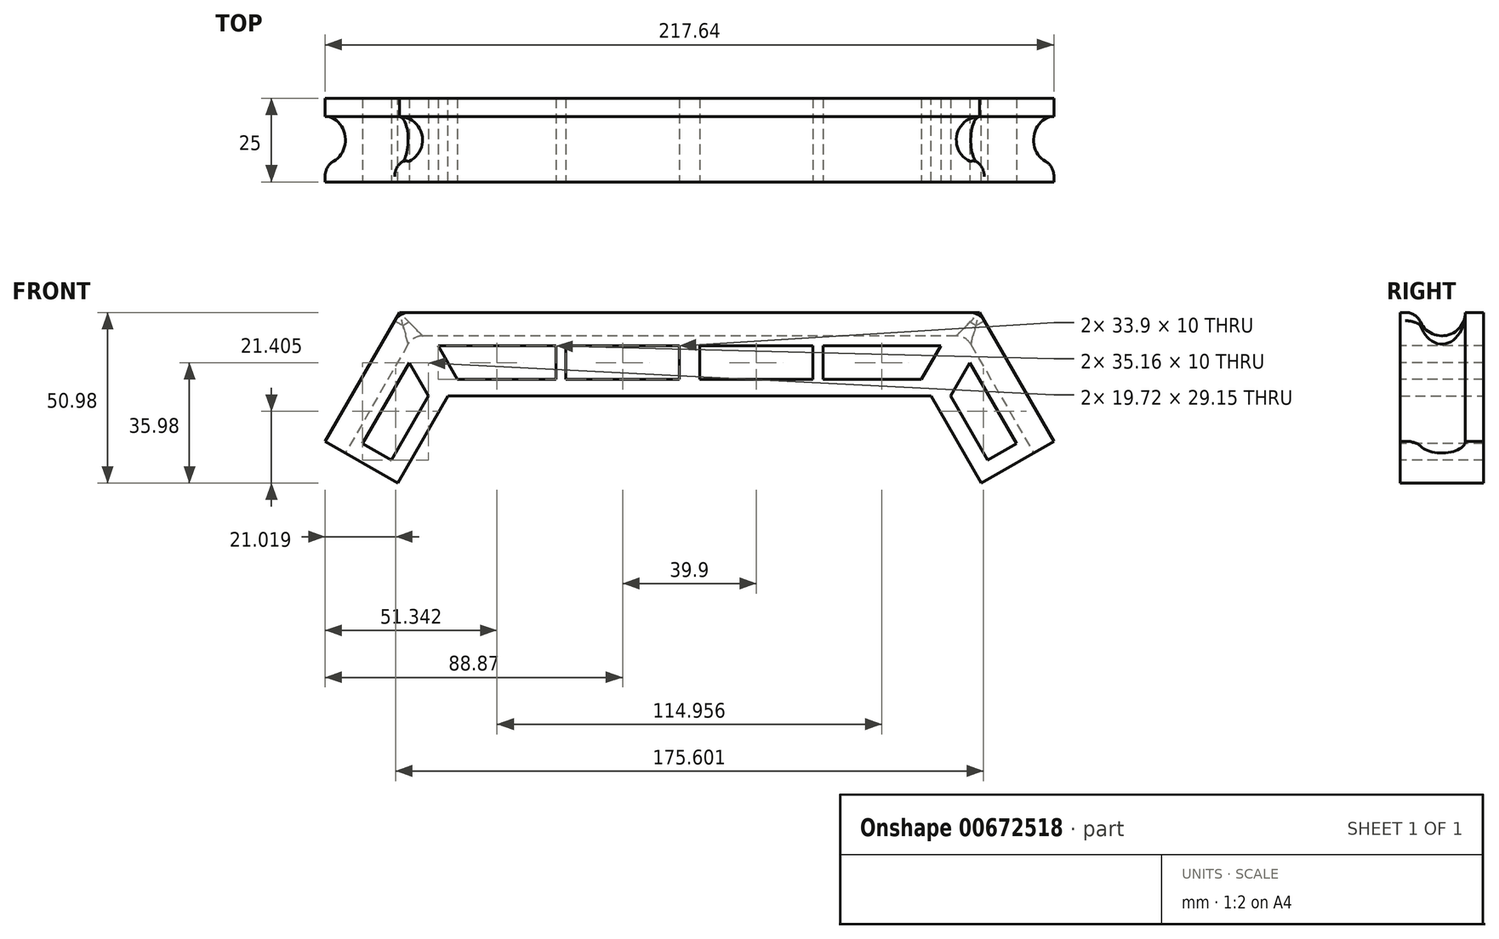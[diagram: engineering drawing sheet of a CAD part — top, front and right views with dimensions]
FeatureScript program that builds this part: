
annotation { "Feature Type Name" : "Feature", "Feature Type Description" : "" }
export const myFeature = defineFeature(function(context is Context, id is Id, definition is map)
    precondition{}
    {
        {
            var Q0;
            Q0=qCreatedBy(makeId("Front.planeOp"),FACE);
            var sketch = newSketch(context, id + "F0", { "sketchPlane" : qUnion([Q0])});
            skCircle(sketch, "E0.cCircle", {"center": v(0, 0) * mm, "radius": 150 * mm, "construction": true});
            skLineSegment(sketch, "E0.0", {"start": v(-86.6, 150) * mm, "end": v(86.6, 150) * mm});
            skLineSegment(sketch, "E0.1", {"start": v(86.6, 150) * mm, "end": v(173.2, 0) * mm});
            skLineSegment(sketch, "E0.2", {"start": v(173.2, 0) * mm, "end": v(86.6, -150) * mm});
            skLineSegment(sketch, "E0.3", {"start": v(86.6, -150) * mm, "end": v(-86.6, -150) * mm});
            skLineSegment(sketch, "E0.4", {"start": v(-86.6, -150) * mm, "end": v(-173.2, 0) * mm});
            skLineSegment(sketch, "E0.5", {"start": v(-173.2, 0) * mm, "end": v(-86.6, 150) * mm});
            skPoint(sketch, "E0.0.midPoint", {"position": v(0, 150) * mm});
            skLineSegment(sketch, "E1.0", {"start": v(72.17, 125) * mm, "end": v(151.55, -12.5) * mm});
            skLineSegment(sketch, "E1.1", {"start": v(-72.17, 125) * mm, "end": v(72.17, 125) * mm});
            skLineSegment(sketch, "E1.2", {"start": v(-151.55, -12.5) * mm, "end": v(-72.17, 125) * mm});
            skLineSegment(sketch, "E2", {"start": v(-87.17, 99.02) * mm, "end": v(-117.44, 116.5) * mm});
            skLineSegment(sketch, "E3", {"start": v(0, 150) * mm, "end": v(0, 125) * mm});
            skSolve(sketch);
        }
        {
            var Q0;
            {var subQ5=sQuery(id+"F0.wireOp",EDGE,"E3");Q0=makeQuery(id+"F0.imprint","IMPRINT",FACE,{"disambiguationData":[TD([[makeQuery(id+"F0.imprint","IMPRINT",EDGE,{"derivedFrom":subQ5}),-1.0]])]});}
            extrude(context, id + "F1", {"entities" : qUnion([Q0]), "depth" : 25 * mm, "offsetDistance" : 25 * mm});
        }
        {
            var Q0;
            Q0=makeQuery(id+"F1.opExtrude","SWEPT_FACE",FACE,{"disambiguationData":[OSD([sQuery(id+"F0.wireOp",EDGE,"E3")])]});
            var sketch = newSketch(context, id + "F2", { "sketchPlane" : qUnion([Q0])});
            skCircle(sketch, "E4", {"center": v(-12.5, 150) * mm, "radius": 7 * mm});
            skPoint(sketch, "E4.centerSnap0", {"position": v(-12.5, 150) * mm});
            skSolve(sketch);
        }
        {
            var Q0;
            {var subQ0=sQuery(id+"F2.wireOp",EDGE,"E4");var subQ1=makeQuery(id+"F1.opExtrude","SWEPT_EDGE",EDGE,{"disambiguationData":[OSD([sQuery(id+"F0.wireOp",EDGE,"E0.0"),sQuery(id+"F0.wireOp",EDGE,"E3")])]});var subQ2=makeQuery(id+"F2.imprint","INTERSECT",VERTEX,{"disambiguationData":[OD(0.0)],"derivedFrom":[subQ1,subQ0]});Q0=makeQuery(id+"F2.imprint","IMPRINT",FACE,{"disambiguationData":[TD([[makeQuery(id+"F2.imprint","IMPRINT",EDGE,{"disambiguationData":[TD([[subQ2,1.0]])],"derivedFrom":subQ0}),1.0]])]});}
            var Q1;
            Q1=makeQuery(id+"F1.opExtrude","CAP_EDGE",EDGE,{"disambiguationData":[OSD([sQuery(id+"F0.wireOp",EDGE,"E0.0")])],"isStart":false});
            var Q2;
            Q2=makeQuery(id+"F1.opExtrude","CAP_EDGE",EDGE,{"disambiguationData":[OSD([sQuery(id+"F0.wireOp",EDGE,"E0.5")])],"isStart":false});
            sweep(context, id + "F3", {"operationType" : NewBodyOperationType.REMOVE, "profiles" : qUnion([Q0]), "path" : qUnion([Q1, Q2])});
        }
        {
            var Q0;
            {var subQ0=makeQuery(id+"F1.opExtrude","CAP_FACE",FACE,{"disambiguationData":[OSD([sQuery(id+"F0.wireOp",EDGE,"E0.0"),sQuery(id+"F0.wireOp",EDGE,"E0.5"),sQuery(id+"F0.wireOp",EDGE,"E1.1"),sQuery(id+"F0.wireOp",EDGE,"E1.2"),sQuery(id+"F0.wireOp",EDGE,"E2"),sQuery(id+"F0.wireOp",EDGE,"E3")])],"isStart":false});Q0=makeQuery(id+"F6.boolean.opBoolean","MERGE",FACE,{"derivedFrom":[subQ0,makeQuery(id+"F6.opPattern","COPY",FACE,{"derivedFrom":subQ0,"instanceName":"1"})]});}
            var sketch = newSketch(context, id + "F4", { "sketchPlane" : qUnion([Q0])});
            skLineSegment(sketch, "E5", {"start": v(-86.6, 150) * mm, "end": v(-72.17, 125) * mm});
            skLineSegment(sketch, "E6.0", {"start": v(-82.27, 152.5) * mm, "end": v(-67.84, 127.5) * mm});
            skLineSegment(sketch, "E7.0", {"start": v(-70.4, 130) * mm, "end": v(70.4, 130) * mm});
            skLineSegment(sketch, "E8.0", {"start": v(-84.88, 140) * mm, "end": v(84.88, 140) * mm});
            skLineSegment(sketch, "E9", {"start": v(0, 140) * mm, "end": v(0, 130) * mm});
            skLineSegment(sketch, "E10", {"start": v(0, 130) * mm, "end": v(-3, 130) * mm});
            skLineSegment(sketch, "E11", {"start": v(-3, 130) * mm, "end": v(-3, 140) * mm});
            skLineSegment(sketch, "E12", {"start": v(-3, 140) * mm, "end": v(0, 140) * mm});
            skLineSegment(sketch, "E13", {"start": v(-36.9, 140) * mm, "end": v(-36.9, 130) * mm});
            skLineSegment(sketch, "E14", {"start": v(-36.9, 130) * mm, "end": v(-39.9, 130) * mm});
            skLineSegment(sketch, "E15", {"start": v(-39.9, 130) * mm, "end": v(-39.9, 140) * mm});
            skLineSegment(sketch, "E16", {"start": v(-39.9, 140) * mm, "end": v(-36.9, 140) * mm});
            skLineSegment(sketch, "E17.0", {"start": v(-84.67, 103.35) * mm, "end": v(-114.94, 120.82) * mm});
            skLineSegment(sketch, "E18.0", {"start": v(-155.88, -10) * mm, "end": v(-75.06, 130) * mm});
            skLineSegment(sketch, "E19", {"start": v(-75.06, 130) * mm, "end": v(-70.4, 130) * mm});
            skLineSegment(sketch, "E20", {"start": v(-80.83, 140) * mm, "end": v(-97.66, 110.85) * mm});
            skLineSegment(sketch, "E21.0", {"start": v(-90.93, 147.5) * mm, "end": v(-76.5, 122.5) * mm});
            skSolve(sketch);
        }
        {
            var Q0;
            {var subQ0=sQuery(id+"F4.wireOp",EDGE,"E20");var subQ1=sQuery(id+"F4.wireOp",EDGE,"E17.0");var subQ2=makeQuery(id+"F4.imprint","INTERSECT",VERTEX,{"derivedFrom":[subQ1,subQ0]});Q0=makeQuery(id+"F4.imprint","IMPRINT",FACE,{"disambiguationData":[TD([[makeQuery(id+"F4.imprint","IMPRINT",EDGE,{"disambiguationData":[TD([[subQ2,1.0]])],"derivedFrom":subQ1}),-1.0]])]});}
            var Q1;
            {var subQ5=sQuery(id+"F4.wireOp",EDGE,"E15");Q1=makeQuery(id+"F4.imprint","IMPRINT",FACE,{"disambiguationData":[TD([[makeQuery(id+"F4.imprint","IMPRINT",EDGE,{"derivedFrom":subQ5}),1.0]])]});}
            var Q2;
            {var subQ0=sQuery(id+"F4.wireOp",EDGE,"E11");Q2=makeQuery(id+"F4.imprint","IMPRINT",FACE,{"disambiguationData":[TD([[makeQuery(id+"F4.imprint","IMPRINT",EDGE,{"derivedFrom":subQ0}),1.0]])]});}
            extrude(context, id + "F5", {"entities" : qUnion([Q0, Q1, Q2]), "operationType" : NewBodyOperationType.REMOVE, "oppositeDirection" : true, "depth" : 25 * mm, "offsetDistance" : 25 * mm});
        }
        {
            var Q0;
            Q0=makeQuery(id+"F1.opExtrude","SWEPT_BODY",BODY,{"disambiguationData":[OSD([sQuery(id+"F0.wireOp",EDGE,"E0.0"),sQuery(id+"F0.wireOp",EDGE,"E0.5"),sQuery(id+"F0.wireOp",EDGE,"E1.1"),sQuery(id+"F0.wireOp",EDGE,"E1.2"),sQuery(id+"F0.wireOp",EDGE,"E2"),sQuery(id+"F0.wireOp",EDGE,"E3")])]});
            var Q1;
            Q1=qCreatedBy(makeId("Right.planeOp"),FACE);
            mirror(context, id + "F6", {"operationType" : NewBodyOperationType.ADD, "entities" : qUnion([Q0]), "mirrorPlane" : qUnion([Q1])});
        }
        {
            var Q0;
            {var subQ0=sQuery(id+"F2.wireOp",EDGE,"E4");var subQ1=sQuery(id+"F0.wireOp",EDGE,"E3");var subQ2=sQuery(id+"F0.wireOp",EDGE,"E0.0");var subQ3=makeQuery(id+"F3.boolean.opBoolean","COPY",EDGE,{"derivedFrom":makeQuery(id+"F3.opSweep","SWEPT_EDGE",EDGE,{"disambiguationData":[OSD([subQ2,subQ1,subQ0]),TDD([makeQuery(id+"F1.opExtrude","CAP_EDGE",EDGE,{"disambiguationData":[OSD([subQ2])],"isStart":false}),makeQuery(id+"F2.imprint","INTERSECT",VERTEX,{"disambiguationData":[OD(1.0)],"derivedFrom":[makeQuery(id+"F1.opExtrude","SWEPT_EDGE",EDGE,{"disambiguationData":[OSD([subQ2,subQ1])]}),subQ0]})])]})});Q0=makeQuery(id+"F6.boolean.opBoolean","MERGE",EDGE,{"derivedFrom":[subQ3,makeQuery(id+"F6.opPattern","COPY",EDGE,{"derivedFrom":subQ3,"instanceName":"1"})]});}
            var Q1;
            {var subQ0=sQuery(id+"F2.wireOp",EDGE,"E4");var subQ1=sQuery(id+"F0.wireOp",EDGE,"E3");var subQ2=sQuery(id+"F0.wireOp",EDGE,"E0.0");var subQ3=sQuery(id+"F0.wireOp",EDGE,"E0.5");Q1=makeQuery(id+"F3.boolean.opBoolean","COPY",EDGE,{"derivedFrom":makeQuery(id+"F3.opSweep","SWEPT_EDGE",EDGE,{"disambiguationData":[OSD([subQ2,subQ3,subQ1,subQ0]),TDD([makeQuery(id+"F1.opExtrude","CAP_EDGE",EDGE,{"disambiguationData":[OSD([subQ3])],"isStart":false}),makeQuery(id+"F2.imprint","INTERSECT",VERTEX,{"disambiguationData":[OD(1.0)],"derivedFrom":[makeQuery(id+"F1.opExtrude","SWEPT_EDGE",EDGE,{"disambiguationData":[OSD([subQ2,subQ1])]}),subQ0]})])]})});}
            var Q2;
            {var subQ0=sQuery(id+"F2.wireOp",EDGE,"E4");var subQ1=sQuery(id+"F0.wireOp",EDGE,"E3");var subQ2=sQuery(id+"F0.wireOp",EDGE,"E0.0");var subQ3=sQuery(id+"F0.wireOp",EDGE,"E0.5");Q2=makeQuery(id+"F6.opPattern","COPY",EDGE,{"derivedFrom":makeQuery(id+"F3.boolean.opBoolean","COPY",EDGE,{"derivedFrom":makeQuery(id+"F3.opSweep","SWEPT_EDGE",EDGE,{"disambiguationData":[OSD([subQ2,subQ3,subQ1,subQ0]),TDD([makeQuery(id+"F1.opExtrude","CAP_EDGE",EDGE,{"disambiguationData":[OSD([subQ3])],"isStart":false}),makeQuery(id+"F2.imprint","INTERSECT",VERTEX,{"disambiguationData":[OD(1.0)],"derivedFrom":[makeQuery(id+"F1.opExtrude","SWEPT_EDGE",EDGE,{"disambiguationData":[OSD([subQ2,subQ1])]}),subQ0]})])]})}),"instanceName":"1"});}
            var Q3;
            {var subQ0=sQuery(id+"F2.wireOp",EDGE,"E4");var subQ1=sQuery(id+"F0.wireOp",EDGE,"E3");var subQ2=sQuery(id+"F0.wireOp",EDGE,"E0.0");var subQ3=sQuery(id+"F0.wireOp",EDGE,"E0.5");Q3=makeQuery(id+"F6.opPattern","COPY",EDGE,{"derivedFrom":makeQuery(id+"F3.boolean.opBoolean","COPY",EDGE,{"derivedFrom":makeQuery(id+"F3.opSweep","SWEPT_EDGE",EDGE,{"disambiguationData":[OSD([subQ2,subQ3,subQ1,subQ0]),TDD([makeQuery(id+"F1.opExtrude","CAP_EDGE",EDGE,{"disambiguationData":[OSD([subQ3])],"isStart":false}),makeQuery(id+"F2.imprint","INTERSECT",VERTEX,{"disambiguationData":[OD(0.0)],"derivedFrom":[makeQuery(id+"F1.opExtrude","SWEPT_EDGE",EDGE,{"disambiguationData":[OSD([subQ2,subQ1])]}),subQ0]})])]})}),"instanceName":"1"});}
            var Q4;
            {var subQ0=sQuery(id+"F2.wireOp",EDGE,"E4");var subQ1=sQuery(id+"F0.wireOp",EDGE,"E3");var subQ2=sQuery(id+"F0.wireOp",EDGE,"E0.0");var subQ3=makeQuery(id+"F3.boolean.opBoolean","COPY",EDGE,{"derivedFrom":makeQuery(id+"F3.opSweep","SWEPT_EDGE",EDGE,{"disambiguationData":[OSD([subQ2,subQ1,subQ0]),TDD([makeQuery(id+"F1.opExtrude","CAP_EDGE",EDGE,{"disambiguationData":[OSD([subQ2])],"isStart":false}),makeQuery(id+"F2.imprint","INTERSECT",VERTEX,{"disambiguationData":[OD(0.0)],"derivedFrom":[makeQuery(id+"F1.opExtrude","SWEPT_EDGE",EDGE,{"disambiguationData":[OSD([subQ2,subQ1])]}),subQ0]})])]})});Q4=makeQuery(id+"F6.boolean.opBoolean","MERGE",EDGE,{"derivedFrom":[subQ3,makeQuery(id+"F6.opPattern","COPY",EDGE,{"derivedFrom":subQ3,"instanceName":"1"})]});}
            var Q5;
            {var subQ0=sQuery(id+"F2.wireOp",EDGE,"E4");var subQ1=sQuery(id+"F0.wireOp",EDGE,"E3");var subQ2=sQuery(id+"F0.wireOp",EDGE,"E0.0");var subQ3=sQuery(id+"F0.wireOp",EDGE,"E0.5");Q5=makeQuery(id+"F3.boolean.opBoolean","COPY",EDGE,{"derivedFrom":makeQuery(id+"F3.opSweep","SWEPT_EDGE",EDGE,{"disambiguationData":[OSD([subQ2,subQ3,subQ1,subQ0]),TDD([makeQuery(id+"F1.opExtrude","CAP_EDGE",EDGE,{"disambiguationData":[OSD([subQ3])],"isStart":false}),makeQuery(id+"F2.imprint","INTERSECT",VERTEX,{"disambiguationData":[OD(0.0)],"derivedFrom":[makeQuery(id+"F1.opExtrude","SWEPT_EDGE",EDGE,{"disambiguationData":[OSD([subQ2,subQ1])]}),subQ0]})])]})});}
            fillet(context, id + "F7", {"entities" : qUnion([Q0, Q1, Q2, Q3, Q4, Q5]), "radius" : 5 * mm, "tangentPropagation" : true, "allowEdgeOverflow" : false});
        }
        {
            var Q0;
            Q0=makeQuery(id+"F3.boolean.opBoolean","COPY",EDGE,{"derivedFrom":makeQuery(id+"F3.opSweep","MID_CAP_EDGE",EDGE,{"disambiguationData":[OSD([sQuery(id+"F0.wireOp",EDGE,"E0.0"),sQuery(id+"F0.wireOp",EDGE,"E0.5"),sQuery(id+"F2.wireOp",EDGE,"E4")])],"capPos":1.0})});
            var Q1;
            Q1=makeQuery(id+"F6.opPattern","COPY",EDGE,{"derivedFrom":makeQuery(id+"F3.boolean.opBoolean","COPY",EDGE,{"derivedFrom":makeQuery(id+"F3.opSweep","MID_CAP_EDGE",EDGE,{"disambiguationData":[OSD([sQuery(id+"F0.wireOp",EDGE,"E0.0"),sQuery(id+"F0.wireOp",EDGE,"E0.5"),sQuery(id+"F2.wireOp",EDGE,"E4")])],"capPos":1.0})}),"instanceName":"1"});
            fillet(context, id + "F8", {"entities" : qUnion([Q0, Q1]), "radius" : 5 * mm, "tangentPropagation" : true, "allowEdgeOverflow" : false});
        }
    });
